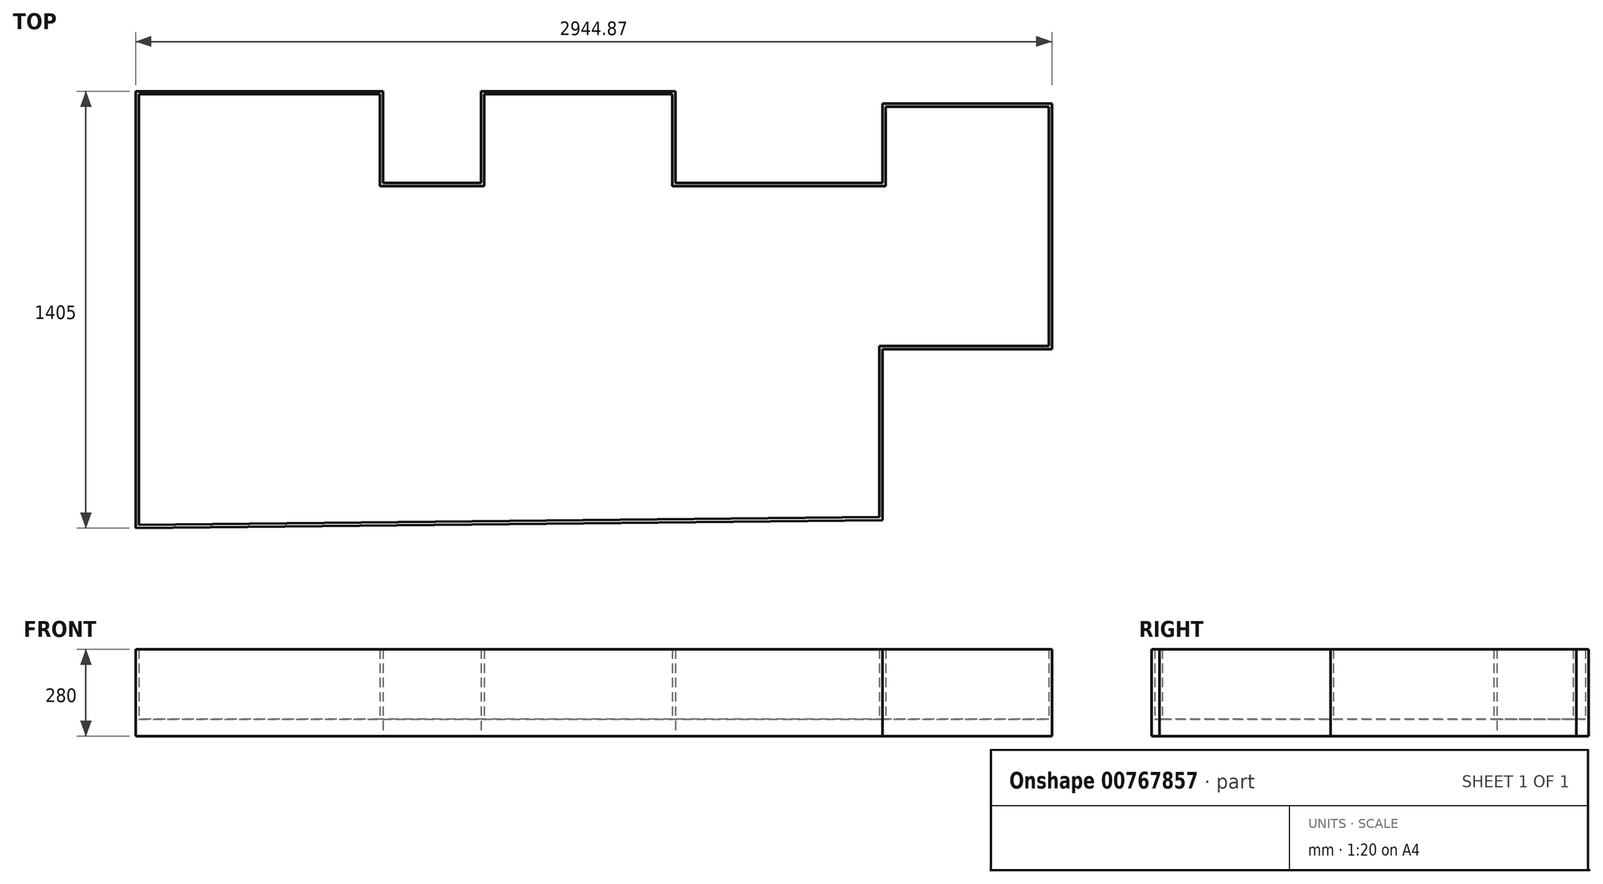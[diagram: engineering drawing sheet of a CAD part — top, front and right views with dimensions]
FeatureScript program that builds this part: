
annotation { "Feature Type Name" : "Feature", "Feature Type Description" : "" }
export const myFeature = defineFeature(function(context is Context, id is Id, definition is map)
    precondition{}
    {
        {
            var Q0;
            Q0=qCreatedBy(makeId("Top.planeOp"),FACE);
            var sketch = newSketch(context, id + "F0", { "sketchPlane" : qUnion([Q0])});
            skLineSegment(sketch, "E0.bottom", {"start": v(0, 0) * mm, "end": v(795, 0) * mm});
            skLineSegment(sketch, "E0.top", {"start": v(0, 0) * mm, "end": v(795, 0) * mm});
            skLineSegment(sketch, "E0.left", {"start": v(0, 0) * mm, "end": v(0, 0) * mm});
            skLineSegment(sketch, "E0.right", {"start": v(795, 0) * mm, "end": v(795, 0) * mm});
            skLineSegment(sketch, "E1.top", {"start": v(795, -295) * mm, "end": v(795, -295) * mm});
            skLineSegment(sketch, "E1.left", {"start": v(795, 0) * mm, "end": v(795, -295) * mm});
            skLineSegment(sketch, "E1.right", {"start": v(795, 0) * mm, "end": v(795, -295) * mm});
            skLineSegment(sketch, "E2.bottom", {"start": v(795, -295) * mm, "end": v(1110, -295) * mm});
            skLineSegment(sketch, "E2.top", {"start": v(795, -295) * mm, "end": v(1110, -295) * mm});
            skLineSegment(sketch, "E2.right", {"start": v(1110, -295) * mm, "end": v(1110, -295) * mm});
            skLineSegment(sketch, "E3.top", {"start": v(1110, 0) * mm, "end": v(1110, 0) * mm});
            skLineSegment(sketch, "E3.left", {"start": v(1110, -295) * mm, "end": v(1110, 0) * mm});
            skLineSegment(sketch, "E3.right", {"start": v(1110, -295) * mm, "end": v(1110, 0) * mm});
            skLineSegment(sketch, "E4.bottom", {"start": v(1110, 0) * mm, "end": v(1735, 0) * mm});
            skLineSegment(sketch, "E4.top", {"start": v(1110, 0) * mm, "end": v(1735, 0) * mm});
            skLineSegment(sketch, "E4.right", {"start": v(1735, 0) * mm, "end": v(1735, 0) * mm});
            skLineSegment(sketch, "E5.top", {"start": v(1735, -295) * mm, "end": v(1735, -295) * mm});
            skLineSegment(sketch, "E5.left", {"start": v(1735, 0) * mm, "end": v(1735, -295) * mm});
            skLineSegment(sketch, "E5.right", {"start": v(1735, 0) * mm, "end": v(1735, -295) * mm});
            skLineSegment(sketch, "E6.bottom", {"start": v(1735, -295) * mm, "end": v(2400, -295) * mm});
            skLineSegment(sketch, "E6.top", {"start": v(1735, -295) * mm, "end": v(2400, -295) * mm});
            skLineSegment(sketch, "E6.right", {"start": v(2400, -295) * mm, "end": v(2400, -295) * mm});
            skLineSegment(sketch, "E7.top", {"start": v(2400, -40) * mm, "end": v(2400, -40) * mm});
            skLineSegment(sketch, "E7.left", {"start": v(2400, -295) * mm, "end": v(2400, -40) * mm});
            skLineSegment(sketch, "E7.right", {"start": v(2400, -295) * mm, "end": v(2400, -40) * mm});
            skLineSegment(sketch, "E8.bottom", {"start": v(2400, -40) * mm, "end": v(2945, -40) * mm});
            skLineSegment(sketch, "E8.top", {"start": v(2400, -40) * mm, "end": v(2945, -40) * mm});
            skLineSegment(sketch, "E8.right", {"start": v(2945, -40) * mm, "end": v(2945, -40) * mm});
            skLineSegment(sketch, "E9.top", {"start": v(2945, -830) * mm, "end": v(2945, -830) * mm});
            skLineSegment(sketch, "E9.left", {"start": v(2945, -40) * mm, "end": v(2945, -830) * mm});
            skLineSegment(sketch, "E9.right", {"start": v(2945, -40) * mm, "end": v(2945, -830) * mm});
            skLineSegment(sketch, "E10.right", {"start": v(2400, -830) * mm, "end": v(2400, -1380) * mm});
            skLineSegment(sketch, "E11.right", {"start": v(0, -1355.02) * mm, "end": v(0.13, -1405) * mm});
            skLineSegment(sketch, "E12.bottom", {"start": v(0, -1405) * mm, "end": v(0.13, -1405) * mm});
            skLineSegment(sketch, "E12.top", {"start": v(0, 0) * mm, "end": v(0.13, 0) * mm});
            skLineSegment(sketch, "E12.left", {"start": v(0.13, -1405) * mm, "end": v(0.13, 0) * mm});
            skLineSegment(sketch, "E12.right", {"start": v(0, -1405) * mm, "end": v(0, 0) * mm});
            skLineSegment(sketch, "E13", {"start": v(2400, -830) * mm, "end": v(2945, -830) * mm});
            skLineSegment(sketch, "E14", {"start": v(0.13, -1405) * mm, "end": v(2400, -1380) * mm});
            skSolve(sketch);
        }
        {
            var Q0;
            {var subQ2=sQuery(id+"F0.wireOp",EDGE,"E1.left");Q0=makeQuery(id+"F0.imprint","IMPRINT",FACE,{"disambiguationData":[TD([[makeQuery(id+"F0.imprint","IMPRINT",EDGE,{"derivedFrom":subQ2}),-1.0]])]});}
            extrude(context, id + "F1", {"entities" : qUnion([Q0]), "depth" : 55 * mm, "offsetDistance" : 25 * mm});
        }
        {
            var Q0;
            Q0=makeQuery(id+"F1.opExtrude","CAP_FACE",FACE,{"disambiguationData":[OSD([sQuery(id+"F0.wireOp",EDGE,"E0.bottom"),sQuery(id+"F0.wireOp",EDGE,"E1.left"),sQuery(id+"F0.wireOp",EDGE,"E2.bottom"),sQuery(id+"F0.wireOp",EDGE,"E3.left"),sQuery(id+"F0.wireOp",EDGE,"E4.bottom"),sQuery(id+"F0.wireOp",EDGE,"E5.left"),sQuery(id+"F0.wireOp",EDGE,"E6.bottom"),sQuery(id+"F0.wireOp",EDGE,"E7.left"),sQuery(id+"F0.wireOp",EDGE,"E8.bottom"),sQuery(id+"F0.wireOp",EDGE,"E9.left"),sQuery(id+"F0.wireOp",EDGE,"E10.right"),sQuery(id+"F0.wireOp",EDGE,"E12.left"),sQuery(id+"F0.wireOp",EDGE,"E13"),sQuery(id+"F0.wireOp",EDGE,"E14")])],"isStart":false});
            var sketch = newSketch(context, id + "F2", { "sketchPlane" : qUnion([Q0])});
            skLineSegment(sketch, "E15", {"start": v(0.13, 0) * mm, "end": v(795, 0) * mm});
            skLineSegment(sketch, "E16", {"start": v(795, 0) * mm, "end": v(795, -295) * mm});
            skLineSegment(sketch, "E17", {"start": v(795, -295) * mm, "end": v(1110, -295) * mm});
            skLineSegment(sketch, "E18", {"start": v(1110, -295) * mm, "end": v(1110, 0) * mm});
            skLineSegment(sketch, "E19", {"start": v(1110, 0) * mm, "end": v(1735, 0) * mm});
            skLineSegment(sketch, "E20", {"start": v(1735, 0) * mm, "end": v(1735, -295) * mm});
            skLineSegment(sketch, "E21", {"start": v(1735, -295) * mm, "end": v(2400, -295) * mm});
            skLineSegment(sketch, "E22", {"start": v(2400, -295) * mm, "end": v(2400, -40) * mm});
            skLineSegment(sketch, "E23", {"start": v(2400, -40) * mm, "end": v(2945, -40) * mm});
            skLineSegment(sketch, "E24", {"start": v(2945, -40) * mm, "end": v(2945, -830) * mm});
            skLineSegment(sketch, "E25", {"start": v(2945, -830) * mm, "end": v(2400, -830) * mm});
            skLineSegment(sketch, "E26", {"start": v(2400, -830) * mm, "end": v(2400, -1380) * mm});
            skLineSegment(sketch, "E27", {"start": v(2400, -1380) * mm, "end": v(0.13, -1405) * mm});
            skLineSegment(sketch, "E28", {"start": v(0.13, -1405) * mm, "end": v(0.13, 0) * mm});
            skLineSegment(sketch, "E29.0", {"start": v(785, -10) * mm, "end": v(10.13, -10) * mm});
            skLineSegment(sketch, "E29.1", {"start": v(785, -305) * mm, "end": v(785, -10) * mm});
            skLineSegment(sketch, "E29.2", {"start": v(1120, -305) * mm, "end": v(785, -305) * mm});
            skLineSegment(sketch, "E29.3", {"start": v(2935, -820) * mm, "end": v(2935, -50) * mm});
            skLineSegment(sketch, "E29.4", {"start": v(2390, -820) * mm, "end": v(2935, -820) * mm});
            skLineSegment(sketch, "E29.5", {"start": v(2390, -1370.1) * mm, "end": v(2390, -820) * mm});
            skLineSegment(sketch, "E29.6", {"start": v(10.13, -1394.9) * mm, "end": v(2390, -1370.1) * mm});
            skLineSegment(sketch, "E29.7", {"start": v(2935, -50) * mm, "end": v(2410, -50) * mm});
            skLineSegment(sketch, "E29.8", {"start": v(2410, -50) * mm, "end": v(2410, -305) * mm});
            skLineSegment(sketch, "E29.9", {"start": v(2410, -305) * mm, "end": v(1725, -305) * mm});
            skLineSegment(sketch, "E29.10", {"start": v(10.13, -10) * mm, "end": v(10.13, -1394.9) * mm});
            skLineSegment(sketch, "E29.11", {"start": v(1725, -305) * mm, "end": v(1725, -10) * mm});
            skLineSegment(sketch, "E29.12", {"start": v(1725, -10) * mm, "end": v(1120, -10) * mm});
            skLineSegment(sketch, "E29.13", {"start": v(1120, -10) * mm, "end": v(1120, -305) * mm});
            skSolve(sketch);
        }
        {
            var Q0;
            Q0 = qSketchRegion(id + "F2", true);
            extrude(context, id + "F3", {"entities" : qUnion([Q0]), "operationType" : NewBodyOperationType.ADD, "depth" : 225 * mm, "offsetDistance" : 25 * mm});
        }
    });
